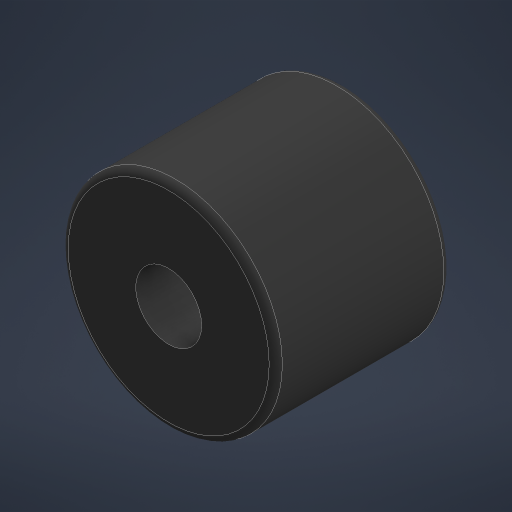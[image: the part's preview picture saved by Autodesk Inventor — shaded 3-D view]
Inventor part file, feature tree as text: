
AUTODESK INVENTOR PART (.ipt)
format: ipt  version: 2023 (Build 270158000, 158)  size: 184,832 bytes
history: native  units: mm
features: extrude x1, fillet x1, sketch x1
ambient origin geometry x8: Origin, YZ Plane, XZ Plane, XY Plane, X Axis, Y Axis, Z Axis, Center Point
bodies: Solid1 (feature_tree)
feature tree (3):
  extrude  "Extrusion1"  Depth=2.0mm
  fillet  "Fillet1"  Radius=53.0mm
  sketch  "Sketch1"  dims[d0=65.0mm d1=20.0mm d2=53.0mm d3=0.0mm d4=2.0mm]
